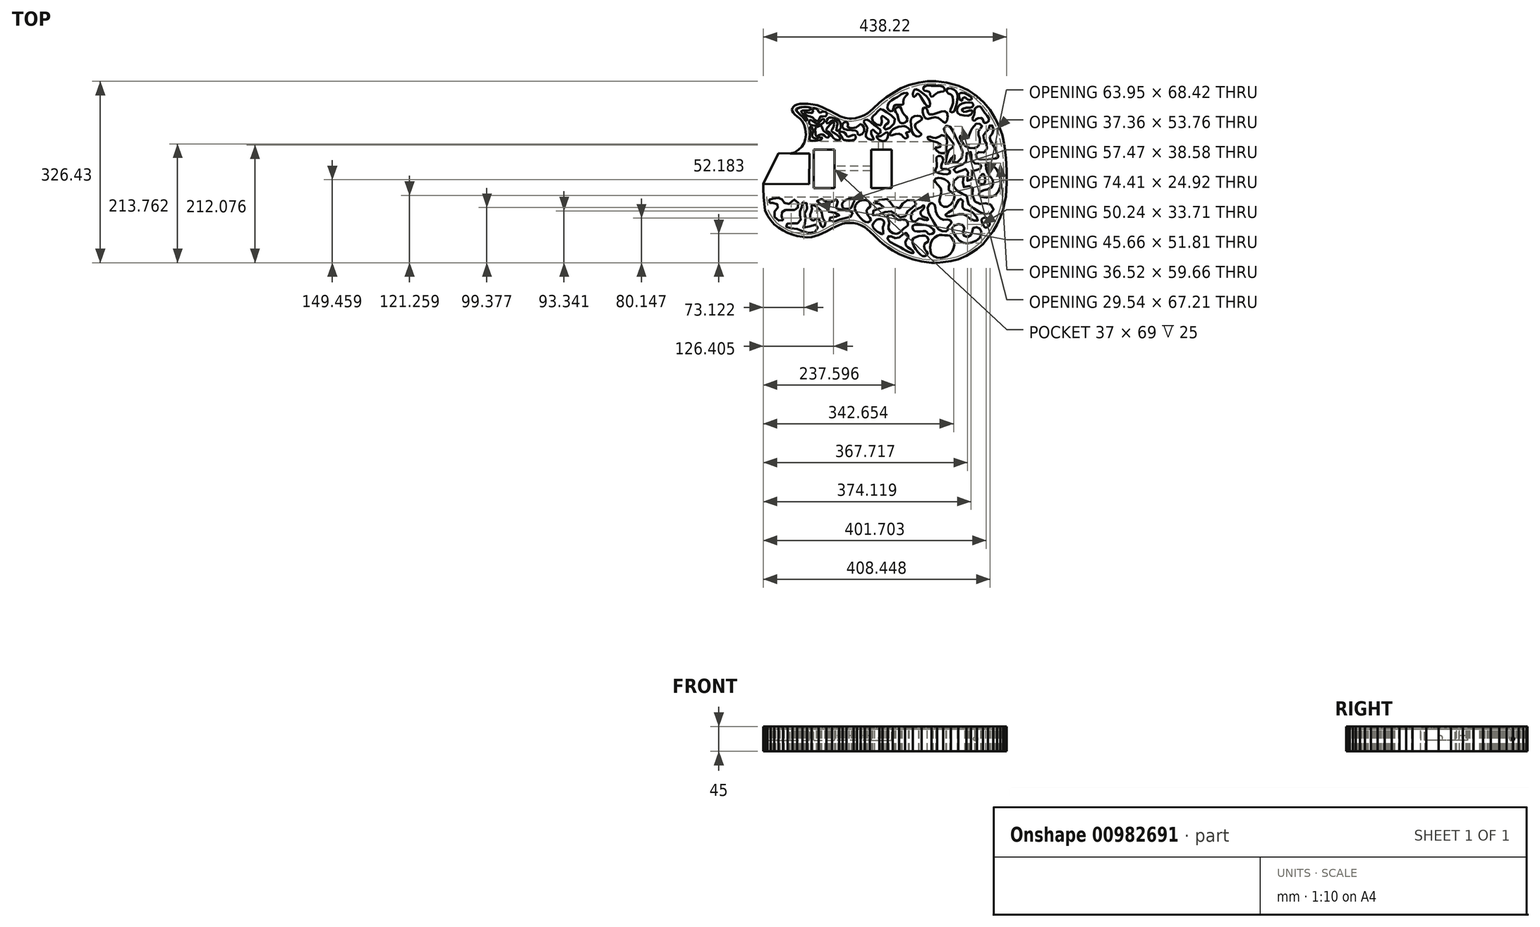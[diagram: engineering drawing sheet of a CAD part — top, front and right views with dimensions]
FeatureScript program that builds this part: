
annotation { "Feature Type Name" : "Feature", "Feature Type Description" : "" }
export const myFeature = defineFeature(function(context is Context, id is Id, definition is map)
    precondition{}
    {
        {
            var Q0;
            Q0=qCreatedBy(makeId("Top.planeOp"),FACE);
            var sketch = newSketch(context, id + "F0", { "sketchPlane" : qUnion([Q0])});
            skLineSegment(sketch, "E0", {"start": v(99.64, 0) * mm, "end": v(99.64, 10.73) * mm});
            skLineSegment(sketch, "E1", {"start": v(99.64, 10.73) * mm, "end": v(98.67, 32.9) * mm});
            skLineSegment(sketch, "E2", {"start": v(98.67, 32.9) * mm, "end": v(95.96, 54.65) * mm});
            skLineSegment(sketch, "E3", {"start": v(95.96, 54.65) * mm, "end": v(91.85, 73.91) * mm});
            skLineSegment(sketch, "E4", {"start": v(91.85, 73.91) * mm, "end": v(85.9, 91) * mm});
            skLineSegment(sketch, "E5", {"start": v(85.9, 91) * mm, "end": v(78.97, 104.86) * mm});
            skLineSegment(sketch, "E6", {"start": v(78.97, 104.86) * mm, "end": v(69.56, 119.79) * mm});
            skLineSegment(sketch, "E7", {"start": v(69.56, 119.79) * mm, "end": v(58.42, 133.1) * mm});
            skLineSegment(sketch, "E8", {"start": v(58.42, 133.1) * mm, "end": v(45.54, 144.89) * mm});
            skLineSegment(sketch, "E9", {"start": v(45.54, 144.89) * mm, "end": v(31.37, 154.73) * mm});
            skLineSegment(sketch, "E10", {"start": v(31.37, 154.73) * mm, "end": v(13.08, 163.28) * mm});
            skLineSegment(sketch, "E11", {"start": v(13.08, 163.28) * mm, "end": v(-8.34, 168.9) * mm});
            skLineSegment(sketch, "E12", {"start": v(-8.34, 168.9) * mm, "end": v(-27.06, 170.96) * mm});
            skLineSegment(sketch, "E13", {"start": v(-27.06, 170.96) * mm, "end": v(-43.5, 170.96) * mm});
            skLineSegment(sketch, "E14", {"start": v(-43.5, 170.96) * mm, "end": v(-58.54, 168.9) * mm});
            skLineSegment(sketch, "E15", {"start": v(-58.54, 168.9) * mm, "end": v(-77.15, 164.04) * mm});
            skLineSegment(sketch, "E16", {"start": v(-77.15, 164.04) * mm, "end": v(-90.67, 158.41) * mm});
            skLineSegment(sketch, "E17", {"start": v(-90.67, 158.41) * mm, "end": v(-102.57, 151.81) * mm});
            skLineSegment(sketch, "E18", {"start": v(-102.57, 151.81) * mm, "end": v(-117.4, 141.86) * mm});
            skLineSegment(sketch, "E19", {"start": v(-117.4, 141.86) * mm, "end": v(-129.08, 132.88) * mm});
            skLineSegment(sketch, "E20", {"start": v(-129.08, 132.88) * mm, "end": v(-141.3, 121.73) * mm});
            skLineSegment(sketch, "E21", {"start": v(-141.3, 121.73) * mm, "end": v(-150.5, 113.73) * mm});
            skLineSegment(sketch, "E22", {"start": v(-150.5, 113.73) * mm, "end": v(-157.64, 109.5) * mm});
            skLineSegment(sketch, "E23", {"start": v(-157.64, 109.5) * mm, "end": v(-164.24, 106.91) * mm});
            skLineSegment(sketch, "E24", {"start": v(-164.24, 106.91) * mm, "end": v(-172.58, 104.86) * mm});
            skLineSegment(sketch, "E25", {"start": v(-172.58, 104.86) * mm, "end": v(-179.46, 103.91) * mm});
            skLineSegment(sketch, "E26", {"start": v(-179.46, 103.91) * mm, "end": v(-183.84, 103.91) * mm});
            skLineSegment(sketch, "E27", {"start": v(-183.84, 103.91) * mm, "end": v(-191.3, 105.29) * mm});
            skLineSegment(sketch, "E28", {"start": v(-191.3, 105.29) * mm, "end": v(-199.42, 107.78) * mm});
            skLineSegment(sketch, "E29", {"start": v(-199.42, 107.78) * mm, "end": v(-207.97, 112.1) * mm});
            skLineSegment(sketch, "E30", {"start": v(-207.97, 112.1) * mm, "end": v(-218.68, 118.16) * mm});
            skLineSegment(sketch, "E31", {"start": v(-218.68, 118.16) * mm, "end": v(-225.4, 121.4) * mm});
            skLineSegment(sketch, "E32", {"start": v(-225.4, 121.4) * mm, "end": v(-233.3, 124.87) * mm});
            skLineSegment(sketch, "E33", {"start": v(-233.3, 124.87) * mm, "end": v(-241.3, 127.8) * mm});
            skLineSegment(sketch, "E34", {"start": v(-241.3, 127.8) * mm, "end": v(-249.1, 129.41) * mm});
            skLineSegment(sketch, "E35", {"start": v(-249.1, 129.41) * mm, "end": v(-257.75, 130.5) * mm});
            skLineSegment(sketch, "E36", {"start": v(-257.75, 130.5) * mm, "end": v(-265.86, 130.5) * mm});
            skLineSegment(sketch, "E37", {"start": v(-265.86, 130.5) * mm, "end": v(-272.14, 130.5) * mm});
            skLineSegment(sketch, "E38", {"start": v(-272.14, 130.5) * mm, "end": v(-277.44, 129.2) * mm});
            skLineSegment(sketch, "E39", {"start": v(-277.44, 129.2) * mm, "end": v(-281.88, 127.25) * mm});
            skLineSegment(sketch, "E40", {"start": v(-281.88, 127.25) * mm, "end": v(-284.58, 125.09) * mm});
            skLineSegment(sketch, "E41", {"start": v(-284.58, 125.09) * mm, "end": v(-285.88, 122.7) * mm});
            skLineSegment(sketch, "E42", {"start": v(-285.88, 122.7) * mm, "end": v(-286.97, 120.11) * mm});
            skLineSegment(sketch, "E43", {"start": v(-286.97, 120.11) * mm, "end": v(-286.2, 118.16) * mm});
            skLineSegment(sketch, "E44", {"start": v(-286.2, 118.16) * mm, "end": v(-284.7, 114.92) * mm});
            skLineSegment(sketch, "E45", {"start": v(-284.7, 114.92) * mm, "end": v(-281.77, 111.89) * mm});
            skLineSegment(sketch, "E46", {"start": v(-281.77, 111.89) * mm, "end": v(-277.44, 107.88) * mm});
            skLineSegment(sketch, "E47", {"start": v(-277.44, 107.88) * mm, "end": v(-272.68, 103.88) * mm});
            skLineSegment(sketch, "E48", {"start": v(-272.68, 103.88) * mm, "end": v(-268.03, 98.58) * mm});
            skLineSegment(sketch, "E49", {"start": v(-268.03, 98.58) * mm, "end": v(-264.57, 92.41) * mm});
            skLineSegment(sketch, "E50", {"start": v(-264.57, 92.41) * mm, "end": v(-262.73, 85.38) * mm});
            skLineSegment(sketch, "E51", {"start": v(-262.73, 85.38) * mm, "end": v(-261.78, 74.51) * mm});
            skLineSegment(sketch, "E52", {"start": v(-261.78, 74.51) * mm, "end": v(-262.75, 67.05) * mm});
            skLineSegment(sketch, "E53", {"start": v(-262.75, 67.05) * mm, "end": v(-264, 63.33) * mm});
            skLineSegment(sketch, "E54", {"start": v(-265.13, 60.01) * mm, "end": v(-269.24, 53.2) * mm});
            skLineSegment(sketch, "E55", {"start": v(-269.24, 53.2) * mm, "end": v(-274.98, 48) * mm});
            skLineSegment(sketch, "E56", {"start": v(-274.98, 48) * mm, "end": v(-282.23, 43.24) * mm});
            skLineSegment(sketch, "E57", {"start": v(-282.23, 43.24) * mm, "end": v(-290.16, 41.2) * mm});
            skLineSegment(sketch, "E58", {"start": v(-311.14, 41.44) * mm, "end": v(-338.55, -13.56) * mm});
            skLineSegment(sketch, "E59", {"start": v(-338.55, -13.56) * mm, "end": v(-338.55, -21.68) * mm});
            skLineSegment(sketch, "E60", {"start": v(-338.55, -21.68) * mm, "end": v(-337.73, -37.51) * mm});
            skLineSegment(sketch, "E61", {"start": v(-335.04, -61.02) * mm, "end": v(-330.72, -70.54) * mm});
            skLineSegment(sketch, "E62", {"start": v(-330.72, -70.54) * mm, "end": v(-325.2, -79.1) * mm});
            skLineSegment(sketch, "E63", {"start": v(-325.2, -79.1) * mm, "end": v(-318.81, -86.34) * mm});
            skLineSegment(sketch, "E64", {"start": v(-318.81, -86.34) * mm, "end": v(-311.14, -92.56) * mm});
            skLineSegment(sketch, "E65", {"start": v(-311.14, -92.56) * mm, "end": v(-302.73, -97.47) * mm});
            skLineSegment(sketch, "E66", {"start": v(-302.73, -97.47) * mm, "end": v(-294.86, -101.8) * mm});
            skLineSegment(sketch, "E67", {"start": v(-294.86, -101.8) * mm, "end": v(-286.1, -105.26) * mm});
            skLineSegment(sketch, "E68", {"start": v(-286.1, -105.26) * mm, "end": v(-277.44, -107.2) * mm});
            skLineSegment(sketch, "E69", {"start": v(-277.44, -107.2) * mm, "end": v(-268.15, -109.07) * mm});
            skLineSegment(sketch, "E70", {"start": v(-268.15, -109.07) * mm, "end": v(-259.64, -109.9) * mm});
            skLineSegment(sketch, "E71", {"start": v(-259.64, -109.9) * mm, "end": v(-251.7, -109.38) * mm});
            skLineSegment(sketch, "E72", {"start": v(-251.7, -109.38) * mm, "end": v(-238.5, -105.78) * mm});
            skLineSegment(sketch, "E73", {"start": v(-238.5, -105.78) * mm, "end": v(-224.86, -99.4) * mm});
            skLineSegment(sketch, "E74", {"start": v(-224.86, -99.4) * mm, "end": v(-214.58, -93.23) * mm});
            skLineSegment(sketch, "E75", {"start": v(-214.58, -93.23) * mm, "end": v(-201.7, -87.6) * mm});
            skLineSegment(sketch, "E76", {"start": v(-201.7, -87.6) * mm, "end": v(-195.32, -85.22) * mm});
            skLineSegment(sketch, "E77", {"start": v(-195.32, -85.22) * mm, "end": v(-188.5, -83.7) * mm});
            skLineSegment(sketch, "E78", {"start": v(-188.5, -83.7) * mm, "end": v(-182, -83.7) * mm});
            skLineSegment(sketch, "E79", {"start": v(-182, -83.7) * mm, "end": v(-175.95, -83.7) * mm});
            skLineSegment(sketch, "E80", {"start": v(-175.95, -83.7) * mm, "end": v(-169.78, -85.33) * mm});
            skLineSegment(sketch, "E81", {"start": v(-169.78, -85.33) * mm, "end": v(-162.96, -88.03) * mm});
            skLineSegment(sketch, "E82", {"start": v(-162.96, -88.03) * mm, "end": v(-155.93, -91.82) * mm});
            skLineSegment(sketch, "E83", {"start": v(-155.93, -91.82) * mm, "end": v(-146.95, -98.96) * mm});
            skLineSegment(sketch, "E84", {"start": v(-146.95, -98.96) * mm, "end": v(-138.61, -107.08) * mm});
            skLineSegment(sketch, "E85", {"start": v(-138.61, -107.08) * mm, "end": v(-129.85, -115.62) * mm});
            skLineSegment(sketch, "E86", {"start": v(-129.85, -115.62) * mm, "end": v(-123.57, -120.92) * mm});
            skLineSegment(sketch, "E87", {"start": v(-123.57, -120.92) * mm, "end": v(-114.59, -127.63) * mm});
            skLineSegment(sketch, "E88", {"start": v(-114.59, -127.63) * mm, "end": v(-105.4, -133.48) * mm});
            skLineSegment(sketch, "E89", {"start": v(-105.4, -133.48) * mm, "end": v(-94.14, -139.75) * mm});
            skLineSegment(sketch, "E90", {"start": v(-94.14, -139.75) * mm, "end": v(-83.53, -144.62) * mm});
            skLineSegment(sketch, "E91", {"start": v(-83.53, -144.62) * mm, "end": v(-69.47, -149.7) * mm});
            skLineSegment(sketch, "E92", {"start": v(-69.47, -149.7) * mm, "end": v(-53.67, -153.5) * mm});
            skLineSegment(sketch, "E93", {"start": v(-53.67, -153.5) * mm, "end": v(-43.93, -154.57) * mm});
            skLineSegment(sketch, "E94", {"start": v(-43.93, -154.57) * mm, "end": v(-35.83, -155.47) * mm});
            skLineSegment(sketch, "E95", {"start": v(-35.83, -155.47) * mm, "end": v(-25.53, -155.47) * mm});
            skLineSegment(sketch, "E96", {"start": v(-25.53, -155.47) * mm, "end": v(-14.82, -154.57) * mm});
            skLineSegment(sketch, "E97", {"start": v(-14.82, -154.57) * mm, "end": v(-0.86, -152.73) * mm});
            skLineSegment(sketch, "E98", {"start": v(-0.86, -152.73) * mm, "end": v(12.77, -149.27) * mm});
            skLineSegment(sketch, "E99", {"start": v(12.77, -149.27) * mm, "end": v(27.17, -143.32) * mm});
            skLineSegment(sketch, "E100", {"start": v(27.17, -143.32) * mm, "end": v(35.82, -138.24) * mm});
            skLineSegment(sketch, "E101", {"start": v(35.82, -138.24) * mm, "end": v(46.43, -130.77) * mm});
            skLineSegment(sketch, "E102", {"start": v(46.43, -130.77) * mm, "end": v(56.82, -122.12) * mm});
            skLineSegment(sketch, "E103", {"start": v(56.82, -122.12) * mm, "end": v(66.34, -110.97) * mm});
            skLineSegment(sketch, "E104", {"start": v(66.34, -110.97) * mm, "end": v(75.32, -98.85) * mm});
            skLineSegment(sketch, "E105", {"start": v(75.32, -98.85) * mm, "end": v(82.68, -86.3) * mm});
            skLineSegment(sketch, "E106", {"start": v(82.68, -86.3) * mm, "end": v(88.2, -73.97) * mm});
            skLineSegment(sketch, "E107", {"start": v(88.2, -73.97) * mm, "end": v(93.18, -59.69) * mm});
            skLineSegment(sketch, "E108", {"start": v(93.18, -59.69) * mm, "end": v(96.1, -47.35) * mm});
            skLineSegment(sketch, "E109", {"start": v(96.1, -47.35) * mm, "end": v(98.37, -36.1) * mm});
            skLineSegment(sketch, "E110", {"start": v(98.37, -36.1) * mm, "end": v(99.67, -11.33) * mm});
            skLineSegment(sketch, "E111", {"start": v(99.67, -11.33) * mm, "end": v(99.64, 0) * mm});
            skLineSegment(sketch, "E112", {"start": v(-311.14, 41.44) * mm, "end": v(-276.44, 41.06) * mm});
            skLineSegment(sketch, "E113", {"start": v(-255.37, 40.83) * mm, "end": v(-255.97, -14.3) * mm});
            skLineSegment(sketch, "E114", {"start": v(-338.55, -13.56) * mm, "end": v(-255.97, -14.3) * mm});
            skLineSegment(sketch, "E115.bottom", {"start": v(-247.47, 47.83) * mm, "end": v(-210.47, 47.83) * mm});
            skLineSegment(sketch, "E115.top", {"start": v(-247.47, -21.17) * mm, "end": v(-210.47, -21.17) * mm});
            skLineSegment(sketch, "E115.left", {"start": v(-247.47, 47.83) * mm, "end": v(-247.47, -21.17) * mm});
            skLineSegment(sketch, "E115.right", {"start": v(-210.47, 47.83) * mm, "end": v(-210.47, -21.17) * mm});
            skLineSegment(sketch, "E116.bottom", {"start": v(-144.47, 47.83) * mm, "end": v(-107.47, 47.83) * mm});
            skLineSegment(sketch, "E116.top", {"start": v(-144.47, -21.17) * mm, "end": v(-107.47, -21.17) * mm});
            skLineSegment(sketch, "E116.left", {"start": v(-144.47, 47.83) * mm, "end": v(-144.47, -21.17) * mm});
            skLineSegment(sketch, "E116.right", {"start": v(-107.47, 47.83) * mm, "end": v(-107.47, -21.17) * mm});
            skLineSegment(sketch, "E117.top", {"start": v(-32.47, -37.51) * mm, "end": v(-337.73, -37.51) * mm});
            skLineSegment(sketch, "E117.left", {"start": v(-32.47, 62.49) * mm, "end": v(-32.47, -37.51) * mm});
            skLineSegment(sketch, "E118", {"start": v(-337.73, -37.51) * mm, "end": v(-335.04, -61.02) * mm});
            skLineSegment(sketch, "E119", {"start": v(-264, 63.33) * mm, "end": v(-265.13, 60.01) * mm});
            skLineSegment(sketch, "E120", {"start": v(-264, 63.33) * mm, "end": v(-32.47, 62.49) * mm});
            skLineSegment(sketch, "E121.2", {"start": v(-265.34, 49.98) * mm, "end": v(-271.91, 44.04) * mm});
            skLineSegment(sketch, "E121.3", {"start": v(-260.57, 57.9) * mm, "end": v(-265.34, 49.98) * mm});
            skLineSegment(sketch, "E121.4", {"start": v(-259.27, 61.73) * mm, "end": v(-260.57, 57.9) * mm});
            skLineSegment(sketch, "E121.5", {"start": v(-257.86, 65.9) * mm, "end": v(-259.27, 61.73) * mm});
            skLineSegment(sketch, "E121.6", {"start": v(-256.75, 74.4) * mm, "end": v(-257.86, 65.9) * mm});
            skLineSegment(sketch, "E121.7", {"start": v(-257.78, 86.24) * mm, "end": v(-256.75, 74.4) * mm});
            skLineSegment(sketch, "E121.8", {"start": v(-259.9, 94.3) * mm, "end": v(-257.78, 86.24) * mm});
            skLineSegment(sketch, "E121.9", {"start": v(-263.93, 101.48) * mm, "end": v(-259.9, 94.3) * mm});
            skLineSegment(sketch, "E121.10", {"start": v(-269.17, 107.46) * mm, "end": v(-263.93, 101.48) * mm});
            skLineSegment(sketch, "E121.11", {"start": v(-274.13, 111.64) * mm, "end": v(-269.17, 107.46) * mm});
            skLineSegment(sketch, "E121.12", {"start": v(-278.27, 115.46) * mm, "end": v(-274.13, 111.64) * mm});
            skLineSegment(sketch, "E121.13", {"start": v(-280.52, 117.79) * mm, "end": v(-278.27, 115.46) * mm});
            skLineSegment(sketch, "E121.14", {"start": v(-281.57, 120.05) * mm, "end": v(-280.52, 117.79) * mm});
            skLineSegment(sketch, "E121.15", {"start": v(-281.37, 120.54) * mm, "end": v(-281.57, 120.05) * mm});
            skLineSegment(sketch, "E121.16", {"start": v(-280.68, 121.81) * mm, "end": v(-281.37, 120.54) * mm});
            skLineSegment(sketch, "E121.17", {"start": v(-279.27, 122.94) * mm, "end": v(-280.68, 121.81) * mm});
            skLineSegment(sketch, "E121.18", {"start": v(-275.83, 124.45) * mm, "end": v(-279.27, 122.94) * mm});
            skLineSegment(sketch, "E121.19", {"start": v(-271.54, 125.5) * mm, "end": v(-275.83, 124.45) * mm});
            skLineSegment(sketch, "E121.20", {"start": v(-265.86, 125.5) * mm, "end": v(-271.54, 125.5) * mm});
            skLineSegment(sketch, "E121.21", {"start": v(-258.06, 125.5) * mm, "end": v(-265.86, 125.5) * mm});
            skLineSegment(sketch, "E121.22", {"start": v(-249.91, 124.48) * mm, "end": v(-258.06, 125.5) * mm});
            skLineSegment(sketch, "E121.23", {"start": v(-242.67, 122.97) * mm, "end": v(-249.91, 124.48) * mm});
            skLineSegment(sketch, "E121.24", {"start": v(-235.15, 120.23) * mm, "end": v(-242.67, 122.97) * mm});
            skLineSegment(sketch, "E121.25", {"start": v(-227.49, 116.87) * mm, "end": v(-235.15, 120.23) * mm});
            skLineSegment(sketch, "E121.26", {"start": v(-221, 113.73) * mm, "end": v(-227.49, 116.87) * mm});
            skLineSegment(sketch, "E121.27", {"start": v(-210.33, 107.7) * mm, "end": v(-221, 113.73) * mm});
            skLineSegment(sketch, "E121.28", {"start": v(-201.3, 103.12) * mm, "end": v(-210.33, 107.7) * mm});
            skLineSegment(sketch, "E121.29", {"start": v(-192.5, 100.42) * mm, "end": v(-201.3, 103.12) * mm});
            skLineSegment(sketch, "E121.30", {"start": v(-184.3, 98.91) * mm, "end": v(-192.5, 100.42) * mm});
            skLineSegment(sketch, "E121.31", {"start": v(-179.12, 98.91) * mm, "end": v(-184.3, 98.91) * mm});
            skLineSegment(sketch, "E121.32", {"start": v(-171.64, 99.94) * mm, "end": v(-179.12, 98.91) * mm});
            skLineSegment(sketch, "E121.33", {"start": v(-162.72, 102.14) * mm, "end": v(-171.64, 99.94) * mm});
            skLineSegment(sketch, "E121.34", {"start": v(-155.44, 105) * mm, "end": v(-162.72, 102.14) * mm});
            skLineSegment(sketch, "E121.35", {"start": v(-147.57, 109.66) * mm, "end": v(-155.44, 105) * mm});
            skLineSegment(sketch, "E121.36", {"start": v(-137.98, 118) * mm, "end": v(-147.57, 109.66) * mm});
            skLineSegment(sketch, "E121.37", {"start": v(-125.87, 129.04) * mm, "end": v(-137.98, 118) * mm});
            skLineSegment(sketch, "E121.38", {"start": v(-114.48, 137.8) * mm, "end": v(-125.87, 129.04) * mm});
            skLineSegment(sketch, "E121.39", {"start": v(-99.96, 147.54) * mm, "end": v(-114.48, 137.8) * mm});
            skLineSegment(sketch, "E121.40", {"start": v(71.14, -96.1) * mm, "end": v(78.23, -84.01) * mm});
            skLineSegment(sketch, "E121.41", {"start": v(62.43, -107.85) * mm, "end": v(71.14, -96.1) * mm});
            skLineSegment(sketch, "E121.42", {"start": v(53.3, -118.54) * mm, "end": v(62.43, -107.85) * mm});
            skLineSegment(sketch, "E121.43", {"start": v(43.38, -126.8) * mm, "end": v(53.3, -118.54) * mm});
            skLineSegment(sketch, "E121.44", {"start": v(33.11, -134.03) * mm, "end": v(43.38, -126.8) * mm});
            skLineSegment(sketch, "E121.45", {"start": v(24.93, -138.83) * mm, "end": v(33.11, -134.03) * mm});
            skLineSegment(sketch, "E121.46", {"start": v(11.2, -144.51) * mm, "end": v(24.93, -138.83) * mm});
            skLineSegment(sketch, "E121.47", {"start": v(-1.8, -147.82) * mm, "end": v(11.2, -144.51) * mm});
            skLineSegment(sketch, "E121.48", {"start": v(-15.36, -149.6) * mm, "end": v(-1.8, -147.82) * mm});
            skLineSegment(sketch, "E121.49", {"start": v(-25.74, -150.47) * mm, "end": v(-15.36, -149.6) * mm});
            skLineSegment(sketch, "E121.50", {"start": v(-35.55, -150.47) * mm, "end": v(-25.74, -150.47) * mm});
            skLineSegment(sketch, "E121.51", {"start": v(-43.38, -149.6) * mm, "end": v(-35.55, -150.47) * mm});
            skLineSegment(sketch, "E121.52", {"start": v(-120.46, -117) * mm, "end": v(-111.75, -123.51) * mm});
            skLineSegment(sketch, "E121.53", {"start": v(-126.48, -111.92) * mm, "end": v(-120.46, -117) * mm});
            skLineSegment(sketch, "E121.54", {"start": v(-135.12, -103.5) * mm, "end": v(-126.48, -111.92) * mm});
            skLineSegment(sketch, "E121.55", {"start": v(-143.64, -95.2) * mm, "end": v(-135.12, -103.5) * mm});
            skLineSegment(sketch, "E121.56", {"start": v(-111.75, -123.51) * mm, "end": v(-102.83, -129.18) * mm});
            skLineSegment(sketch, "E121.57", {"start": v(-102.83, -129.18) * mm, "end": v(-91.87, -135.29) * mm});
            skLineSegment(sketch, "E121.58", {"start": v(-91.87, -135.29) * mm, "end": v(-81.64, -139.99) * mm});
            skLineSegment(sketch, "E121.59", {"start": v(-81.64, -139.99) * mm, "end": v(-68.03, -144.9) * mm});
            skLineSegment(sketch, "E121.60", {"start": v(-68.03, -144.9) * mm, "end": v(-52.8, -148.56) * mm});
            skLineSegment(sketch, "E121.61", {"start": v(-52.8, -148.56) * mm, "end": v(-43.38, -149.6) * mm});
            skLineSegment(sketch, "E121.62", {"start": v(78.23, -84.01) * mm, "end": v(83.55, -72.12) * mm});
            skLineSegment(sketch, "E121.63", {"start": v(83.55, -72.12) * mm, "end": v(88.37, -58.28) * mm});
            skLineSegment(sketch, "E121.64", {"start": v(88.37, -58.28) * mm, "end": v(91.21, -46.28) * mm});
            skLineSegment(sketch, "E121.65", {"start": v(91.21, -46.28) * mm, "end": v(93.4, -35.47) * mm});
            skLineSegment(sketch, "E121.66", {"start": v(93.4, -35.47) * mm, "end": v(94.67, -11.2) * mm});
            skLineSegment(sketch, "E121.67", {"start": v(94.67, -11.2) * mm, "end": v(94.64, 0) * mm});
            skLineSegment(sketch, "E121.68", {"start": v(94.64, 0) * mm, "end": v(94.64, 10.62) * mm});
            skLineSegment(sketch, "E121.69", {"start": v(94.64, 10.62) * mm, "end": v(93.68, 32.49) * mm});
            skLineSegment(sketch, "E121.70", {"start": v(93.68, 32.49) * mm, "end": v(91.03, 53.82) * mm});
            skLineSegment(sketch, "E121.71", {"start": v(91.03, 53.82) * mm, "end": v(87.02, 72.56) * mm});
            skLineSegment(sketch, "E121.72", {"start": v(87.02, 72.56) * mm, "end": v(81.28, 89.06) * mm});
            skLineSegment(sketch, "E121.73", {"start": v(81.28, 89.06) * mm, "end": v(74.61, 102.4) * mm});
            skLineSegment(sketch, "E121.74", {"start": v(74.61, 102.4) * mm, "end": v(65.51, 116.83) * mm});
            skLineSegment(sketch, "E121.75", {"start": v(65.51, 116.83) * mm, "end": v(54.8, 129.63) * mm});
            skLineSegment(sketch, "E121.76", {"start": v(54.8, 129.63) * mm, "end": v(42.41, 140.97) * mm});
            skLineSegment(sketch, "E121.77", {"start": v(42.41, 140.97) * mm, "end": v(28.87, 150.38) * mm});
            skLineSegment(sketch, "E121.78", {"start": v(28.87, 150.38) * mm, "end": v(11.38, 158.56) * mm});
            skLineSegment(sketch, "E121.79", {"start": v(11.38, 158.56) * mm, "end": v(-9.25, 163.98) * mm});
            skLineSegment(sketch, "E121.80", {"start": v(-9.25, 163.98) * mm, "end": v(-27.33, 165.96) * mm});
            skLineSegment(sketch, "E121.81", {"start": v(-27.33, 165.96) * mm, "end": v(-43.16, 165.96) * mm});
            skLineSegment(sketch, "E121.82", {"start": v(-43.16, 165.96) * mm, "end": v(-57.56, 164) * mm});
            skLineSegment(sketch, "E121.83", {"start": v(-57.56, 164) * mm, "end": v(-75.55, 159.29) * mm});
            skLineSegment(sketch, "E121.84", {"start": v(-75.55, 159.29) * mm, "end": v(-88.5, 153.9) * mm});
            skLineSegment(sketch, "E121.85", {"start": v(-88.5, 153.9) * mm, "end": v(-99.96, 147.54) * mm});
            skLineSegment(sketch, "E122.0", {"start": v(-153.16, -87.63) * mm, "end": v(-143.64, -95.2) * mm});
            skLineSegment(sketch, "E122.1", {"start": v(-160.85, -83.5) * mm, "end": v(-153.16, -87.63) * mm});
            skLineSegment(sketch, "E122.2", {"start": v(-168.21, -80.57) * mm, "end": v(-160.85, -83.5) * mm});
            skLineSegment(sketch, "E122.3", {"start": v(-175.3, -78.7) * mm, "end": v(-168.21, -80.57) * mm});
            skLineSegment(sketch, "E122.4", {"start": v(-182, -78.7) * mm, "end": v(-175.3, -78.7) * mm});
            skLineSegment(sketch, "E122.5", {"start": v(-252.53, -104.42) * mm, "end": v(-240.22, -101.07) * mm});
            skLineSegment(sketch, "E122.6", {"start": v(-259.56, -104.89) * mm, "end": v(-252.53, -104.42) * mm});
            skLineSegment(sketch, "E122.7", {"start": v(-267.41, -104.12) * mm, "end": v(-259.56, -104.89) * mm});
            skLineSegment(sketch, "E122.8", {"start": v(-276.4, -102.31) * mm, "end": v(-267.41, -104.12) * mm});
            skLineSegment(sketch, "E122.9", {"start": v(-240.22, -101.07) * mm, "end": v(-227.2, -94.97) * mm});
            skLineSegment(sketch, "E122.10", {"start": v(-227.2, -94.97) * mm, "end": v(-216.87, -88.77) * mm});
            skLineSegment(sketch, "E122.11", {"start": v(-216.87, -88.77) * mm, "end": v(-203.58, -82.96) * mm});
            skLineSegment(sketch, "E122.12", {"start": v(-203.58, -82.96) * mm, "end": v(-196.74, -80.42) * mm});
            skLineSegment(sketch, "E122.13", {"start": v(-196.74, -80.42) * mm, "end": v(-189.05, -78.7) * mm});
            skLineSegment(sketch, "E122.14", {"start": v(-189.05, -78.7) * mm, "end": v(-182, -78.7) * mm});
            skLineSegment(sketch, "E123.0", {"start": v(-284.62, -100.46) * mm, "end": v(-276.4, -102.31) * mm});
            skLineSegment(sketch, "E123.1", {"start": v(-292.73, -97.26) * mm, "end": v(-284.62, -100.46) * mm});
            skLineSegment(sketch, "E123.2", {"start": v(-300.26, -93.12) * mm, "end": v(-292.73, -97.26) * mm});
            skLineSegment(sketch, "E123.3", {"start": v(-308.29, -88.44) * mm, "end": v(-300.26, -93.12) * mm});
            skLineSegment(sketch, "E123.4", {"start": v(-315.34, -82.72) * mm, "end": v(-308.29, -88.44) * mm});
            skLineSegment(sketch, "E123.5", {"start": v(-332.7, -37.51) * mm, "end": v(-330.17, -59.67) * mm});
            skLineSegment(sketch, "E123.6", {"start": v(-330.17, -59.67) * mm, "end": v(-326.32, -68.14) * mm});
            skLineSegment(sketch, "E123.7", {"start": v(-326.32, -68.14) * mm, "end": v(-321.2, -76.07) * mm});
            skLineSegment(sketch, "E123.8", {"start": v(-321.2, -76.07) * mm, "end": v(-315.34, -82.72) * mm});
            skLineSegment(sketch, "E124", {"start": v(-276.44, 41.06) * mm, "end": v(-255.37, 40.83) * mm});
            skLineSegment(sketch, "E125", {"start": v(-271.91, 44.04) * mm, "end": v(-276.44, 41.06) * mm});
            skSolve(sketch);
        }
        {
            var Q0;
            {var subQ1=sQuery(id+"F0.wireOp",EDGE,"E117.left");Q0=makeQuery(id+"F0.imprint","IMPRINT",FACE,{"disambiguationData":[TD([[makeQuery(id+"F0.imprint","IMPRINT",EDGE,{"derivedFrom":subQ1}),1.0]])]});}
            extrude(context, id + "F1", {"entities" : qUnion([Q0]), "oppositeDirection" : true, "depth" : 5 * mm, "offsetDistance" : 25 * mm});
        }
        {
            var Q0;
            Q0=makeQuery(id+"F0.imprint","IMPRINT",FACE,{"disambiguationData":[TD([[makeQuery(id+"F0.imprint","IMPRINT",EDGE,{"derivedFrom":sQuery(id+"F0.wireOp",EDGE,"E116.bottom")}),-1.0]])]});
            var Q1;
            Q1=makeQuery(id+"F0.imprint","IMPRINT",FACE,{"disambiguationData":[TD([[makeQuery(id+"F0.imprint","IMPRINT",EDGE,{"derivedFrom":sQuery(id+"F0.wireOp",EDGE,"E115.bottom")}),-1.0]])]});
            var Q2;
            {var subQ2=sQuery(id+"F0.wireOp",EDGE,"E58");Q2=makeQuery(id+"F0.imprint","IMPRINT",FACE,{"disambiguationData":[TD([[makeQuery(id+"F0.imprint","IMPRINT",EDGE,{"derivedFrom":subQ2}),1.0]])]});}
            var Q3;
            Q3=makeQuery(id+"F0.imprint","IMPRINT",FACE,{"disambiguationData":[TD([[makeQuery(id+"F0.imprint","IMPRINT",EDGE,{"derivedFrom":sQuery(id+"F0.wireOp",EDGE,"E54")}),1.0]])]});
            var Q4;
            Q4=makeQuery(id+"F0.imprint","IMPRINT",FACE,{"disambiguationData":[TD([[makeQuery(id+"F0.imprint","IMPRINT",EDGE,{"derivedFrom":sQuery(id+"F0.wireOp",EDGE,"E0")}),1.0]])]});
            var Q5;
            Q5=makeQuery(id+"F0.imprint","IMPRINT",FACE,{"disambiguationData":[TD([[makeQuery(id+"F0.imprint","IMPRINT",EDGE,{"derivedFrom":sQuery(id+"F0.wireOp",EDGE,"E59")}),1.0]])]});
            extrude(context, id + "F2", {"entities" : qUnion([Q0, Q1, Q2, Q3, Q4, Q5]), "operationType" : NewBodyOperationType.ADD, "oppositeDirection" : true, "depth" : 45 * mm, "offsetDistance" : 25 * mm});
        }
        {
            var Q0;
            {var subQ3=sQuery(id+"F0.wireOp",EDGE,"E58");Q0=makeQuery(id+"F0.imprint","IMPRINT",FACE,{"disambiguationData":[TD([[makeQuery(id+"F0.imprint","IMPRINT",EDGE,{"derivedFrom":subQ3}),1.0]])]});}
            var Q1;
            Q1=makeQuery(id+"F0.imprint","IMPRINT",FACE,{"disambiguationData":[TD([[makeQuery(id+"F0.imprint","IMPRINT",EDGE,{"derivedFrom":sQuery(id+"F0.wireOp",EDGE,"E115.bottom")}),-1.0]])]});
            var Q2;
            Q2=makeQuery(id+"F0.imprint","IMPRINT",FACE,{"disambiguationData":[TD([[makeQuery(id+"F0.imprint","IMPRINT",EDGE,{"derivedFrom":sQuery(id+"F0.wireOp",EDGE,"E116.bottom")}),-1.0]])]});
            extrude(context, id + "F3", {"entities" : qUnion([Q0, Q1, Q2]), "operationType" : NewBodyOperationType.REMOVE, "oppositeDirection" : true, "depth" : 25 * mm, "offsetDistance" : 25 * mm});
        }
        {
            var Q0;
            Q0=makeQuery(id+"F0.imprint","IMPRINT",FACE,{"disambiguationData":[TD([[makeQuery(id+"F0.imprint","IMPRINT",EDGE,{"derivedFrom":sQuery(id+"F0.wireOp",EDGE,"E0")}),1.0]])]});
            var sketch = newSketch(context, id + "F4", { "sketchPlane" : qUnion([Q0])});
            skFitSpline(sketch, "E126", {"points": [v(-246.67, 91.44) * mm, v(-255.37, 94.7) * mm, v(-254.1, 101.73) * mm, v(-241.7, 95.17) * mm, v(-232.1, 102.95) * mm, v(-228.07, 100.65) * mm, v(-233.02, 94.58) * mm, v(-246.67, 91.44) * mm]});
            skFitSpline(sketch, "E127", {"points": [v(-258.94, 109.16) * mm, v(-251.4, 107.22) * mm, v(-244.58, 100.33) * mm, v(-241.6, 99.56) * mm, v(-238.44, 101.73) * mm, v(-235.53, 107.77) * mm, v(-226.8, 107.66) * mm, v(-223.68, 113.46) * mm, v(-230.26, 116.77) * mm, v(-237.78, 114.71) * mm, v(-240.12, 120) * mm, v(-248.96, 122.42) * mm, v(-249.1, 116) * mm, v(-255.82, 113.94) * mm, v(-264.55, 115.33) * mm, v(-258.94, 109.16) * mm]});
            skFitSpline(sketch, "E128", {"points": [v(-255.87, 119.1) * mm, v(-252.32, 121.73) * mm, v(-256.46, 124.17) * mm, v(-265.55, 124.75) * mm, v(-273.37, 123.7) * mm, v(-278.9, 119.25) * mm, v(-269.9, 109.16) * mm, v(-261.8, 100.15) * mm, v(-258.94, 101.73) * mm, v(-261.8, 105.93) * mm, v(-267.11, 111.9) * mm, v(-270.06, 117.75) * mm, v(-255.87, 119.1) * mm]});
            skFitSpline(sketch, "E129", {"points": [v(-253.77, 75.85) * mm, v(-253.77, 83.98) * mm, v(-255.18, 86.65) * mm, v(-253.91, 89.03) * mm, v(-249.85, 85.38) * mm, v(-248.44, 81.46) * mm, v(-250.4, 72.48) * mm, v(-243.25, 67.85) * mm, v(-237.78, 70.38) * mm, v(-232.45, 69.11) * mm, v(-236.66, 65.05) * mm, v(-245.64, 64.34) * mm, v(-253.07, 64.34) * mm, v(-255.04, 66.45) * mm, v(-253.77, 75.85) * mm]});
            skFitSpline(sketch, "E130", {"points": [v(-228.8, 73.74) * mm, v(-236.24, 75.14) * mm, v(-242.7, 72.06) * mm, v(-244.52, 78.23) * mm, v(-244.38, 87.77) * mm, v(-241.15, 89.31) * mm, v(-234, 91.13) * mm, v(-230.77, 82.72) * mm, v(-219.83, 73.46) * mm, v(-223.76, 69.67) * mm, v(-228.8, 73.74) * mm]});
            skFitSpline(sketch, "E131", {"points": [v(-222.36, 89.03) * mm, v(-224.6, 82.44) * mm, v(-218.7, 77.95) * mm, v(-213.8, 71.08) * mm, v(-206.37, 65.33) * mm, v(-200.06, 67) * mm, v(-204.96, 74.02) * mm, v(-215.62, 81.6) * mm, v(-213.24, 86.65) * mm, v(-211.7, 97.45) * mm, v(-222.36, 89.03) * mm]});
            skFitSpline(sketch, "E132", {"points": [v(-220.67, 96.32) * mm, v(-224.6, 95.9) * mm, v(-223.62, 101.8) * mm, v(-220.4, 105.58) * mm, v(-207.63, 103.62) * mm, v(-200.2, 98.15) * mm, v(-199.92, 85.24) * mm, v(-206.23, 81.74) * mm, v(-206.09, 89.45) * mm, v(-205.1, 96.46) * mm, v(-211.84, 100.95) * mm, v(-220.67, 96.32) * mm]});
            skFitSpline(sketch, "E133", {"points": [v(-197.67, 71.92) * mm, v(-194.3, 66.17) * mm, v(-185.19, 64.77) * mm, v(-172.85, 67.43) * mm, v(-173.97, 74.58) * mm, v(-186.17, 71.5) * mm, v(-191.78, 78.37) * mm, v(-201.46, 79.91) * mm, v(-197.67, 71.92) * mm]});
            skFitSpline(sketch, "E134", {"points": [v(-194.02, 85.52) * mm, v(-169.9, 81.18) * mm, v(-167.8, 74.72) * mm, v(-157, 80.2) * mm, v(-162.33, 93.94) * mm, v(-170.46, 88.75) * mm, v(-186.17, 88.6) * mm, v(-186.17, 95.06) * mm, v(-189.12, 98) * mm, v(-195.15, 95.06) * mm, v(-194.02, 85.52) * mm]});
            skFitSpline(sketch, "E135", {"points": [v(-157.84, 98.43) * mm, v(-150.97, 86.5) * mm, v(-154.47, 74.3) * mm, v(-147.88, 66.59) * mm, v(-139.74, 66.73) * mm, v(-144.23, 76.4) * mm, v(-141.85, 84.12) * mm, v(-131.19, 76.27) * mm, v(-127.12, 81.32) * mm, v(-140.3, 93.52) * mm, v(-148.44, 100.81) * mm, v(-154.2, 101.65) * mm, v(-157.84, 98.43) * mm]});
            skFitSpline(sketch, "E136", {"points": [v(-120.39, 76.97) * mm, v(-127.68, 72.48) * mm, v(-134.27, 72.2) * mm, v(-129.93, 65.75) * mm, v(-117.72, 65.33) * mm, v(-113.94, 78.37) * mm, v(-120.39, 76.97) * mm]});
            skFitSpline(sketch, "E137", {"points": [v(-141.05, 99) * mm, v(-142.24, 106.38) * mm, v(-136.53, 112.18) * mm, v(-127.97, 121.08) * mm, v(-117.38, 116.04) * mm, v(-101.33, 99.74) * mm, v(-118.8, 84.33) * mm, v(-120.63, 90.53) * mm, v(-112.3, 97.85) * mm, v(-118.46, 105.15) * mm, v(-125.7, 108.72) * mm, v(-126.34, 92.27) * mm, v(-141.05, 99) * mm]});
            skFitSpline(sketch, "E138", {"points": [v(-109.75, 73.77) * mm, v(-93.2, 76.7) * mm, v(-82.7, 68.09) * mm, v(-78.03, 72.53) * mm, v(-81.44, 78.57) * mm, v(-74.63, 80.97) * mm, v(-80.37, 89.06) * mm, v(-90.67, 89.93) * mm, v(-106.73, 83.21) * mm, v(-109.75, 73.77) * mm]});
            skFitSpline(sketch, "E139", {"points": [v(-83.15, 96.88) * mm, v(-90.9, 96.09) * mm, v(-95.45, 104.54) * mm, v(-98.4, 113.35) * mm, v(-101.36, 121.37) * mm, v(-92.34, 124.9) * mm, v(-87.06, 114.05) * mm, v(-78.8, 103.9) * mm, v(-83.15, 96.88) * mm]});
            skFitSpline(sketch, "E140", {"points": [v(-94.61, 128.93) * mm, v(-102.8, 127.36) * mm, v(-105.21, 118.3) * mm, v(-112.55, 118.5) * mm, v(-114.7, 127.68) * mm, v(-105.9, 137.57) * mm, v(-94, 144.8) * mm, v(-88.14, 149) * mm, v(-78, 149.53) * mm, v(-86.02, 138.82) * mm, v(-86.45, 129.9) * mm, v(-94.61, 128.93) * mm]});
            skCircle(sketch, "E141", {"center": v(-31.57, 88.37) * mm, "radius": 15.31 * mm});
            skCircle(sketch, "E142", {"center": v(-68.3, 125.46) * mm, "radius": 15.31 * mm});
            skCircle(sketch, "E143", {"center": v(-15.1, 133.37) * mm, "radius": 15.31 * mm});
            skCircle(sketch, "E144", {"center": v(18.97, 93.18) * mm, "radius": 15.31 * mm});
            skFitSpline(sketch, "E145", {"points": [v(-69.32, 147.51) * mm, v(-64.71, 156.72) * mm, v(-50.82, 149) * mm, v(-40, 137.8) * mm, v(-39.54, 125.1) * mm, v(-48.49, 132.08) * mm, v(-57.81, 147.4) * mm, v(-61.97, 147.91) * mm, v(-67.06, 142.89) * mm, v(-69.32, 147.51) * mm]});
            skFitSpline(sketch, "E146", {"points": [v(-51.3, 115.48) * mm, v(-49.7, 123.57) * mm, v(-44.18, 122.24) * mm, v(-40.86, 112.43) * mm, v(-22.94, 114.73) * mm, v(-8.23, 115.53) * mm, v(-9.5, 97.1) * mm, v(-16.78, 99.88) * mm, v(-28.5, 106.74) * mm, v(-44.86, 103.6) * mm, v(-51.3, 115.48) * mm]});
            skFitSpline(sketch, "E147", {"points": [v(-72.77, 99.18) * mm, v(-70.82, 105.48) * mm, v(-58.22, 109.11) * mm, v(-52.41, 103.4) * mm, v(-59.3, 97.83) * mm, v(-65.4, 92.44) * mm, v(-60.7, 82.4) * mm, v(-53.92, 76.06) * mm, v(-59.4, 71.64) * mm, v(-69.55, 77.86) * mm, v(-72.77, 99.18) * mm]});
            skFitSpline(sketch, "E148", {"points": [v(-29.15, 51.59) * mm, v(-21.2, 52.37) * mm, v(-19.27, 57.68) * mm, v(-41.07, 66.4) * mm, v(-42.74, 70.8) * mm, v(-35.8, 70.82) * mm, v(-26.32, 68.98) * mm, v(-15.46, 74.44) * mm, v(-7.72, 66.9) * mm, v(-8.63, 54.82) * mm, v(-10.13, 42.95) * mm, v(-16.52, 41.53) * mm, v(-23.8, 44.1) * mm, v(-29.15, 51.59) * mm]});
            skFitSpline(sketch, "E149", {"points": [v(-4.36, 46.69) * mm, v(4.84, 54.47) * mm, v(-6.72, 72.64) * mm, v(-13.33, 86.55) * mm, v(-6.25, 91.5) * mm, v(3.42, 81.13) * mm, v(9.55, 66.97) * mm, v(19.22, 48.81) * mm, v(15.45, 28.53) * mm, v(3.18, 25.22) * mm, v(6.72, 36.55) * mm, v(4.36, 38.2) * mm, v(-5.54, 22.63) * mm, v(-10.5, 22.63) * mm, v(-8.61, 30.88) * mm, v(-4.36, 46.69) * mm]});
            skFitSpline(sketch, "E150", {"points": [v(-33.85, 143.64) * mm, v(-25.36, 150.48) * mm, v(-12.38, 153.78) * mm, v(-13.8, 160.38) * mm, v(-31.02, 162.98) * mm, v(-49.18, 161.33) * mm, v(-49.18, 154.72) * mm, v(-39.51, 151.9) * mm, v(-37.62, 145.76) * mm, v(-33.85, 143.64) * mm]});
            skFitSpline(sketch, "E151", {"points": [v(2.7, 142.69) * mm, v(0, 147.05) * mm, v(-6.62, 150.23) * mm, v(-7.8, 157.37) * mm, v(1.91, 157.37) * mm, v(9.65, 150.82) * mm, v(11.03, 139.52) * mm, v(8.46, 125.83) * mm, v(3.1, 115.51) * mm, v(-1.86, 116.7) * mm, v(2.1, 128.8) * mm, v(2.7, 142.69) * mm]});
            skFitSpline(sketch, "E152", {"points": [v(17.58, 136.14) * mm, v(13.81, 143.88) * mm, v(15.6, 149.63) * mm, v(26.1, 148.84) * mm, v(37.02, 139.32) * mm, v(29.48, 138.13) * mm, v(24.13, 142.3) * mm, v(19.56, 139.52) * mm, v(19.96, 137.13) * mm, v(17.58, 136.14) * mm]});
            skFitSpline(sketch, "E153", {"points": [v(11.23, 114.32) * mm, v(10.84, 123.05) * mm, v(17.38, 130.2) * mm, v(28.1, 132.97) * mm, v(39.2, 131.18) * mm, v(38.2, 125.23) * mm, v(29.48, 123.65) * mm, v(19.17, 120.08) * mm, v(22.34, 115.91) * mm, v(31.27, 118.3) * mm, v(38.2, 117.7) * mm, v(36.03, 111.35) * mm, v(24.13, 109.56) * mm, v(11.23, 114.32) * mm]});
            skFitSpline(sketch, "E154", {"points": [v(38.01, 103.6) * mm, v(41.78, 112.14) * mm, v(42.18, 121.07) * mm, v(51.1, 126.03) * mm, v(57.25, 118.1) * mm, v(67.96, 100.64) * mm, v(59.04, 96.27) * mm, v(56.26, 103.6) * mm, v(46.14, 103.6) * mm, v(41.38, 100.04) * mm, v(38.01, 103.6) * mm]});
            skFitSpline(sketch, "E155", {"points": [v(25.68, 54.54) * mm, v(17.55, 65.2) * mm, v(15.3, 72.5) * mm, v(21.2, 72.21) * mm, v(29.33, 68.29) * mm, v(33.82, 78.95) * mm, v(39.43, 88.48) * mm, v(47.28, 95.5) * mm, v(55.42, 89.89) * mm, v(48.69, 80.63) * mm, v(51.77, 66.32) * mm, v(45.04, 51.59) * mm, v(25.68, 54.54) * mm]});
            skFitSpline(sketch, "E156", {"points": [v(67.48, 84.84) * mm, v(60.19, 78.1) * mm, v(58.22, 67.73) * mm, v(64.4, 56.79) * mm, v(59.35, 43.04) * mm, v(46.16, 43.32) * mm, v(45.32, 32.38) * mm, v(59.07, 30.98) * mm, v(84.6, 33.78) * mm, v(82.63, 40.52) * mm, v(80.95, 47.8) * mm, v(71.4, 62.68) * mm, v(69.45, 71.37) * mm, v(75.34, 78.95) * mm, v(74.5, 90.45) * mm, v(69.45, 92.13) * mm, v(67.48, 84.84) * mm]});
            skFitSpline(sketch, "E157", {"points": [v(20.35, 21.72) * mm, v(27.65, 29.58) * mm, v(27.65, 41.64) * mm, v(36.34, 43.04) * mm, v(35.5, 33.22) * mm, v(43.92, 22.56) * mm, v(52.33, 22) * mm, v(53.46, 15.27) * mm, v(46.16, 11.62) * mm, v(36.9, 8.54) * mm, v(37.75, -4.09) * mm, v(28.2, -7.45) * mm, v(30.73, 4.33) * mm, v(24.84, 13.3) * mm, v(9.98, 6.85) * mm, v(4.37, 12.75) * mm, v(20.35, 21.72) * mm]});
            skFitSpline(sketch, "E158", {"points": [v(-14.43, 30.42) * mm, v(-18.64, 36.3) * mm, v(-26.5, 33.78) * mm, v(-25.93, 18.08) * mm, v(-29.15, 9.66) * mm, v(-18.36, 4.61) * mm, v(-2.93, 5.73) * mm, v(-4.9, 12.75) * mm, v(-16.4, 13.3) * mm, v(-17.8, 20.88) * mm, v(-14.43, 30.42) * mm]});
            skFitSpline(sketch, "E159", {"points": [v(66.08, 5.45) * mm, v(63, 23.12) * mm, v(79.54, 15.27) * mm, v(88.52, -8.57) * mm, v(85.43, -25.97) * mm, v(70.85, -37.47) * mm, v(50.09, -34.38) * mm, v(53.46, -26.53) * mm, v(72.25, -20.36) * mm, v(74.77, -7.17) * mm, v(66.08, 5.45) * mm]});
            skFitSpline(sketch, "E160", {"points": [v(22.04, 0) * mm, v(21.2, -18.67) * mm, v(37.19, -17.55) * mm, v(38.3, -35.78) * mm, v(51.21, -49.8) * mm, v(66.36, -48.69) * mm, v(76.18, -60.47) * mm, v(62.43, -68.6) * mm, v(45.88, -60.75) * mm, v(29.33, -47.85) * mm, v(29.05, -36.9) * mm, v(18.4, -31.02) * mm, v(4.37, -18.67) * mm, v(7.17, -5.2) * mm, v(22.04, 0) * mm]});
            skFitSpline(sketch, "E161", {"points": [v(50.09, -11.66) * mm, v(56.82, -14.18) * mm, v(61.03, -8.3) * mm, v(57.1, 4.05) * mm, v(49.8, -5.49) * mm, v(50.09, -11.66) * mm]});
            skFitSpline(sketch, "E162", {"points": [v(-28.74, -10.54) * mm, v(-18.08, -24.56) * mm, v(-21.44, -45.88) * mm, v(-10.22, -55.42) * mm, v(3.8, -43.64) * mm, v(4.65, -31.86) * mm, v(-4.61, -24) * mm, v(-3.49, -13.06) * mm, v(-13.87, -4.65) * mm, v(-24.25, -2.96) * mm, v(-30.14, -6.33) * mm, v(-28.74, -10.54) * mm]});
            skFitSpline(sketch, "E163", {"points": [v(-4.84, -64.9) * mm, v(5.26, -57.88) * mm, v(12, -44.14) * mm, v(16.76, -40.5) * mm, v(20.97, -44.7) * mm, v(19.85, -53.68) * mm, v(24.05, -59.57) * mm, v(34.43, -62.93) * mm, v(47.9, -78.92) * mm, v(37.24, -78.38) * mm, v(26.02, -69.95) * mm, v(12, -68.26) * mm, v(-3.44, -72.2) * mm, v(-10.73, -70.23) * mm, v(-4.84, -64.9) * mm]});
            skFitSpline(sketch, "E164", {"points": [v(56.03, -83.97) * mm, v(54.63, -77.52) * mm, v(60.8, -74.44) * mm, v(67.25, -78.08) * mm, v(68.38, -88.18) * mm, v(61.64, -92.39) * mm, v(56.03, -83.97) * mm]});
            skFitSpline(sketch, "E165", {"points": [v(45.1, -115.67) * mm, v(53.23, -108.1) * mm, v(54.07, -99.12) * mm, v(49.3, -92.39) * mm, v(39.76, -92.95) * mm, v(37.24, -101.36) * mm, v(29.33, -109.22) * mm, v(20.97, -104.17) * mm, v(23.21, -91.83) * mm, v(15.64, -85.94) * mm, v(2.46, -90.99) * mm, v(3.02, -99.68) * mm, v(16.76, -117.07) * mm, v(29.33, -120.72) * mm, v(45.1, -115.67) * mm]});
            skFitSpline(sketch, "E166", {"points": [v(-5.68, -96.32) * mm, v(-6.24, -90.14) * mm, v(0, -84.81) * mm, v(-2.6, -78.38) * mm, v(-12.41, -78.38) * mm, v(-21.1, -74.72) * mm, v(-28.68, -60.97) * mm, v(-29.24, -52.56) * mm, v(-36.26, -47.85) * mm, v(-42.43, -57.32) * mm, v(-37.94, -72.47) * mm, v(-31.2, -82.85) * mm, v(-24.2, -94.07) * mm, v(-11.57, -99.4) * mm, v(-5.68, -96.32) * mm]});
            skFitSpline(sketch, "E167", {"points": [v(-25.06, -107.17) * mm, v(-19.4, -105.52) * mm, v(-11.38, -106.23) * mm, v(-4.54, -106.23) * mm, v(2.3, -112.84) * mm, v(5.37, -124.87) * mm, v(0, -137.13) * mm, v(-9.73, -144.92) * mm, v(-24.12, -146.33) * mm, v(-35.2, -140.9) * mm, v(-38.03, -128.88) * mm, v(-34.5, -114.25) * mm, v(-25.06, -107.17) * mm]});
            skFitSpline(sketch, "E168", {"points": [v(-55.25, -141.38) * mm, v(-47.23, -143.74) * mm, v(-42.51, -139.02) * mm, v(-47.7, -131.47) * mm, v(-47.47, -120.62) * mm, v(-41.57, -117.55) * mm, v(-43.93, -108.59) * mm, v(-58.08, -107.65) * mm, v(-68.93, -112.13) * mm, v(-69.17, -121.8) * mm, v(-55.25, -141.38) * mm]});
            skFitSpline(sketch, "E169", {"points": [v(-65.87, -98.68) * mm, v(-46.05, -98.92) * mm, v(-40.16, -104.34) * mm, v(-30.72, -100.1) * mm, v(-41.57, -88.78) * mm, v(-56.9, -86.89) * mm, v(-69.4, -89.25) * mm, v(-65.87, -98.68) * mm]});
            skFitSpline(sketch, "E170", {"points": [v(-54.3, -55.52) * mm, v(-69.17, -63.06) * mm, v(-71.53, -78.38) * mm, v(-64.92, -81.46) * mm, v(-58.32, -76.04) * mm, v(-48.65, -78.38) * mm, v(-41.8, -78.38) * mm, v(-42.75, -75.57) * mm, v(-52.19, -71.8) * mm, v(-55.25, -63.54) * mm, v(-48.65, -56.46) * mm, v(-49.83, -51.98) * mm, v(-54.3, -55.52) * mm]});
            skFitSpline(sketch, "E171", {"points": [v(-91.58, -127.93) * mm, v(-82.85, -133.36) * mm, v(-73.89, -137.37) * mm, v(-68.23, -138.31) * mm, v(-69.88, -133.6) * mm, v(-76.95, -128.64) * mm, v(-82.85, -120.86) * mm, v(-80.02, -112.84) * mm, v(-76.72, -109.06) * mm, v(-81.67, -101.99) * mm, v(-97, -111.18) * mm, v(-111.4, -107.41) * mm, v(-114.7, -112.84) * mm, v(-91.58, -127.93) * mm]});
            skFitSpline(sketch, "E172", {"points": [v(-98.63, -103.63) * mm, v(-86.57, -94.65) * mm, v(-78.15, -87.64) * mm, v(-82.64, -78.38) * mm, v(-95.82, -78.38) * mm, v(-104.8, -70.24) * mm, v(-114.9, -70.52) * mm, v(-111.53, -82.87) * mm, v(-113.22, -94.37) * mm, v(-98.63, -103.63) * mm]});
            skFitSpline(sketch, "E173", {"points": [v(-141.83, -87.92) * mm, v(-130.05, -101.39) * mm, v(-122.47, -103.63) * mm, v(-123.31, -92.97) * mm, v(-120.8, -83.43) * mm, v(-128.36, -76.7) * mm, v(-141.83, -87.92) * mm]});
            skFitSpline(sketch, "E174", {"points": [v(-129.49, -68.56) * mm, v(-116.3, -63.22) * mm, v(-102.56, -65.47) * mm, v(-95.26, -72.2) * mm, v(-83.76, -73.05) * mm, v(-79, -63.22) * mm, v(-68.9, -55.93) * mm, v(-62.72, -47.85) * mm, v(-71.42, -42.18) * mm, v(-86.85, -47.85) * mm, v(-92.74, -57.33) * mm, v(-107.89, -52) * mm, v(-111.25, -43.3) * mm, v(-124.72, -41.34) * mm, v(-139.02, -47.85) * mm, v(-123.31, -51.16) * mm, v(-123.03, -57.05) * mm, v(-136.5, -58.73) * mm, v(-142.67, -68.56) * mm, v(-129.49, -68.56) * mm]});
            skFitSpline(sketch, "E175", {"points": [v(-163.43, -75.3) * mm, v(-151.09, -82.87) * mm, v(-144.63, -78.38) * mm, v(-150.24, -70.24) * mm, v(-151.37, -59.3) * mm, v(-146.04, -54.52) * mm, v(-148.84, -45.26) * mm, v(-161.47, -43.02) * mm, v(-173.8, -55.37) * mm, v(-163.43, -75.3) * mm]});
            skFitSpline(sketch, "E176", {"points": [v(-176.33, -47.85) * mm, v(-181.38, -57.05) * mm, v(-194.57, -56.77) * mm, v(-195.69, -47.85) * mm, v(-186.43, -41.05) * mm, v(-178.3, -39.93) * mm, v(-174.09, -43.58) * mm, v(-176.33, -47.85) * mm]});
            skFitSpline(sketch, "E177", {"points": [v(-207.47, -56.49) * mm, v(-198.5, -60.7) * mm, v(-186.71, -62.1) * mm, v(-180, -62.87) * mm, v(-177.45, -68.56) * mm, v(-184.75, -74.17) * mm, v(-199.33, -76.97) * mm, v(-212.8, -81.74) * mm, v(-220.37, -78.38) * mm, v(-215.04, -73.05) * mm, v(-201.86, -71.36) * mm, v(-205.79, -66.87) * mm, v(-220.65, -63.5) * mm, v(-225.98, -55.37) * mm, v(-241.97, -45.54) * mm, v(-234.68, -40.77) * mm, v(-220.1, -47.85) * mm, v(-210.27, -42.18) * mm, v(-203.82, -42.74) * mm, v(-207.47, -56.49) * mm]});
            skFitSpline(sketch, "E178", {"points": [v(-318.27, -63.22) * mm, v(-311.54, -53.96) * mm, v(-319.11, -47.85) * mm, v(-326.69, -47.85) * mm, v(-328.1, -42.74) * mm, v(-320.24, -40.21) * mm, v(-305.93, -39.93) * mm, v(-300.6, -47.85) * mm, v(-287.98, -47.85) * mm, v(-284.61, -41.9) * mm, v(-275.35, -47.85) * mm, v(-278.44, -59.01) * mm, v(-289.1, -60.42) * mm, v(-300.6, -61.26) * mm, v(-306.5, -68.84) * mm, v(-303.13, -78.38) * mm, v(-313.5, -78.38) * mm, v(-318.27, -63.22) * mm]});
            skFitSpline(sketch, "E179", {"points": [v(-288.26, -93.25) * mm, v(-297.51, -90.16) * mm, v(-295.55, -85.4) * mm, v(-284.05, -85.11) * mm, v(-273.67, -82.87) * mm, v(-271.43, -73.33) * mm, v(-273.67, -65.19) * mm, v(-269.74, -58.73) * mm, v(-268.62, -47.85) * mm, v(-260.77, -47.85) * mm, v(-260.77, -60.98) * mm, v(-264.7, -70.24) * mm, v(-261.6, -78.38) * mm, v(-266.66, -91.85) * mm, v(-253.2, -89.32) * mm, v(-241.41, -88.2) * mm, v(-242.53, -98.68) * mm, v(-259.65, -101.1) * mm, v(-272.83, -96.34) * mm, v(-288.26, -93.25) * mm]});
            skFitSpline(sketch, "E180", {"points": [v(-252.07, -78.38) * mm, v(-253.75, -68.56) * mm, v(-250.95, -59.3) * mm, v(-251.23, -51.16) * mm, v(-241.41, -55.93) * mm, v(-233, -65.75) * mm, v(-231.31, -75.85) * mm, v(-226.54, -83.99) * mm, v(-230.47, -91.85) * mm, v(-235.8, -85.67) * mm, v(-239.45, -75.3) * mm, v(-245.62, -78.38) * mm, v(-252.07, -78.38) * mm]});
            skSolve(sketch);
        }
        {
            var Q0;
            Q0=makeQuery(id+"F4.imprint","IMPRINT",FACE,{"disambiguationData":[TD([[makeQuery(id+"F4.imprint","IMPRINT",EDGE,{"derivedFrom":sQuery(id+"F4.wireOp",EDGE,"E128")}),1.0]])]});
            var Q1;
            Q1=makeQuery(id+"F4.imprint","IMPRINT",FACE,{"disambiguationData":[TD([[makeQuery(id+"F4.imprint","IMPRINT",EDGE,{"derivedFrom":sQuery(id+"F4.wireOp",EDGE,"E127")}),1.0]])]});
            var Q2;
            Q2=makeQuery(id+"F4.imprint","IMPRINT",FACE,{"disambiguationData":[TD([[makeQuery(id+"F4.imprint","IMPRINT",EDGE,{"derivedFrom":sQuery(id+"F4.wireOp",EDGE,"E126")}),-1.0]])]});
            var Q3;
            Q3=makeQuery(id+"F4.imprint","IMPRINT",FACE,{"disambiguationData":[TD([[makeQuery(id+"F4.imprint","IMPRINT",EDGE,{"derivedFrom":sQuery(id+"F4.wireOp",EDGE,"E129")}),-1.0]])]});
            var Q4;
            Q4=makeQuery(id+"F4.imprint","IMPRINT",FACE,{"disambiguationData":[TD([[makeQuery(id+"F4.imprint","IMPRINT",EDGE,{"derivedFrom":sQuery(id+"F4.wireOp",EDGE,"E130")}),-1.0]])]});
            var Q5;
            Q5=makeQuery(id+"F4.imprint","IMPRINT",FACE,{"disambiguationData":[TD([[makeQuery(id+"F4.imprint","IMPRINT",EDGE,{"derivedFrom":sQuery(id+"F4.wireOp",EDGE,"E131")}),1.0]])]});
            var Q6;
            Q6=makeQuery(id+"F4.imprint","IMPRINT",FACE,{"disambiguationData":[TD([[makeQuery(id+"F4.imprint","IMPRINT",EDGE,{"derivedFrom":sQuery(id+"F4.wireOp",EDGE,"E132")}),-1.0]])]});
            var Q7;
            Q7=makeQuery(id+"F4.imprint","IMPRINT",FACE,{"disambiguationData":[TD([[makeQuery(id+"F4.imprint","IMPRINT",EDGE,{"derivedFrom":sQuery(id+"F4.wireOp",EDGE,"E134")}),1.0]])]});
            var Q8;
            Q8=makeQuery(id+"F4.imprint","IMPRINT",FACE,{"disambiguationData":[TD([[makeQuery(id+"F4.imprint","IMPRINT",EDGE,{"derivedFrom":sQuery(id+"F4.wireOp",EDGE,"E133")}),1.0]])]});
            var Q9;
            Q9=makeQuery(id+"F4.imprint","IMPRINT",FACE,{"disambiguationData":[TD([[makeQuery(id+"F4.imprint","IMPRINT",EDGE,{"derivedFrom":sQuery(id+"F4.wireOp",EDGE,"E135")}),1.0]])]});
            var Q10;
            Q10=makeQuery(id+"F4.imprint","IMPRINT",FACE,{"disambiguationData":[TD([[makeQuery(id+"F4.imprint","IMPRINT",EDGE,{"derivedFrom":sQuery(id+"F4.wireOp",EDGE,"E136")}),1.0]])]});
            var Q11;
            Q11=makeQuery(id+"F4.imprint","IMPRINT",FACE,{"disambiguationData":[TD([[makeQuery(id+"F4.imprint","IMPRINT",EDGE,{"derivedFrom":sQuery(id+"F4.wireOp",EDGE,"E137")}),-1.0]])]});
            var Q12;
            Q12=makeQuery(id+"F4.imprint","IMPRINT",FACE,{"disambiguationData":[TD([[makeQuery(id+"F4.imprint","IMPRINT",EDGE,{"derivedFrom":sQuery(id+"F4.wireOp",EDGE,"E138")}),1.0]])]});
            var Q13;
            Q13=makeQuery(id+"F4.imprint","IMPRINT",FACE,{"disambiguationData":[TD([[makeQuery(id+"F4.imprint","IMPRINT",EDGE,{"derivedFrom":sQuery(id+"F4.wireOp",EDGE,"E139")}),-1.0]])]});
            var Q14;
            Q14=makeQuery(id+"F4.imprint","IMPRINT",FACE,{"disambiguationData":[TD([[makeQuery(id+"F4.imprint","IMPRINT",EDGE,{"derivedFrom":sQuery(id+"F4.wireOp",EDGE,"E140")}),-1.0]])]});
            var Q15;
            Q15=makeQuery(id+"F4.imprint","IMPRINT",FACE,{"disambiguationData":[TD([[makeQuery(id+"F4.imprint","IMPRINT",EDGE,{"derivedFrom":sQuery(id+"F4.wireOp",EDGE,"E145")}),-1.0]])]});
            var Q16;
            Q16=makeQuery(id+"F4.imprint","IMPRINT",FACE,{"disambiguationData":[TD([[makeQuery(id+"F4.imprint","IMPRINT",EDGE,{"derivedFrom":sQuery(id+"F4.wireOp",EDGE,"E150")}),1.0]])]});
            var Q17;
            Q17=makeQuery(id+"F4.imprint","IMPRINT",FACE,{"disambiguationData":[TD([[makeQuery(id+"F4.imprint","IMPRINT",EDGE,{"derivedFrom":sQuery(id+"F4.wireOp",EDGE,"E151")}),-1.0]])]});
            var Q18;
            Q18=makeQuery(id+"F4.imprint","IMPRINT",FACE,{"disambiguationData":[TD([[makeQuery(id+"F4.imprint","IMPRINT",EDGE,{"derivedFrom":sQuery(id+"F4.wireOp",EDGE,"E152")}),-1.0]])]});
            var Q19;
            Q19=makeQuery(id+"F4.imprint","IMPRINT",FACE,{"disambiguationData":[TD([[makeQuery(id+"F4.imprint","IMPRINT",EDGE,{"derivedFrom":sQuery(id+"F4.wireOp",EDGE,"E153")}),-1.0]])]});
            var Q20;
            Q20=makeQuery(id+"F4.imprint","IMPRINT",FACE,{"disambiguationData":[TD([[makeQuery(id+"F4.imprint","IMPRINT",EDGE,{"derivedFrom":sQuery(id+"F4.wireOp",EDGE,"E154")}),-1.0]])]});
            var Q21;
            Q21=makeQuery(id+"F4.imprint","IMPRINT",FACE,{"disambiguationData":[TD([[makeQuery(id+"F4.imprint","IMPRINT",EDGE,{"derivedFrom":sQuery(id+"F4.wireOp",EDGE,"E146")}),-1.0]])]});
            var Q22;
            Q22=makeQuery(id+"F4.imprint","IMPRINT",FACE,{"disambiguationData":[TD([[makeQuery(id+"F4.imprint","IMPRINT",EDGE,{"derivedFrom":sQuery(id+"F4.wireOp",EDGE,"E147")}),-1.0]])]});
            var Q23;
            Q23=makeQuery(id+"F4.imprint","IMPRINT",FACE,{"disambiguationData":[TD([[makeQuery(id+"F4.imprint","IMPRINT",EDGE,{"derivedFrom":sQuery(id+"F4.wireOp",EDGE,"E148")}),-1.0]])]});
            var Q24;
            Q24=makeQuery(id+"F4.imprint","IMPRINT",FACE,{"disambiguationData":[TD([[makeQuery(id+"F4.imprint","IMPRINT",EDGE,{"derivedFrom":sQuery(id+"F4.wireOp",EDGE,"E149")}),-1.0]])]});
            var Q25;
            Q25=makeQuery(id+"F4.imprint","IMPRINT",FACE,{"disambiguationData":[TD([[makeQuery(id+"F4.imprint","IMPRINT",EDGE,{"derivedFrom":sQuery(id+"F4.wireOp",EDGE,"E155")}),-1.0]])]});
            var Q26;
            Q26=makeQuery(id+"F4.imprint","IMPRINT",FACE,{"disambiguationData":[TD([[makeQuery(id+"F4.imprint","IMPRINT",EDGE,{"derivedFrom":sQuery(id+"F4.wireOp",EDGE,"E156")}),1.0]])]});
            var Q27;
            Q27=makeQuery(id+"F4.imprint","IMPRINT",FACE,{"disambiguationData":[TD([[makeQuery(id+"F4.imprint","IMPRINT",EDGE,{"derivedFrom":sQuery(id+"F4.wireOp",EDGE,"E157")}),-1.0]])]});
            var Q28;
            Q28=makeQuery(id+"F4.imprint","IMPRINT",FACE,{"disambiguationData":[TD([[makeQuery(id+"F4.imprint","IMPRINT",EDGE,{"derivedFrom":sQuery(id+"F4.wireOp",EDGE,"E158")}),1.0]])]});
            var Q29;
            Q29=makeQuery(id+"F4.imprint","IMPRINT",FACE,{"disambiguationData":[TD([[makeQuery(id+"F4.imprint","IMPRINT",EDGE,{"derivedFrom":sQuery(id+"F4.wireOp",EDGE,"E161")}),1.0]])]});
            var Q30;
            Q30=makeQuery(id+"F4.imprint","IMPRINT",FACE,{"disambiguationData":[TD([[makeQuery(id+"F4.imprint","IMPRINT",EDGE,{"derivedFrom":sQuery(id+"F4.wireOp",EDGE,"E159")}),-1.0]])]});
            var Q31;
            Q31=makeQuery(id+"F4.imprint","IMPRINT",FACE,{"disambiguationData":[TD([[makeQuery(id+"F4.imprint","IMPRINT",EDGE,{"derivedFrom":sQuery(id+"F4.wireOp",EDGE,"E160")}),-1.0]])]});
            var Q32;
            Q32=makeQuery(id+"F4.imprint","IMPRINT",FACE,{"disambiguationData":[TD([[makeQuery(id+"F4.imprint","IMPRINT",EDGE,{"derivedFrom":sQuery(id+"F4.wireOp",EDGE,"E162")}),1.0]])]});
            var Q33;
            Q33=makeQuery(id+"F4.imprint","IMPRINT",FACE,{"disambiguationData":[TD([[makeQuery(id+"F4.imprint","IMPRINT",EDGE,{"derivedFrom":sQuery(id+"F4.wireOp",EDGE,"E163")}),-1.0]])]});
            var Q34;
            Q34=makeQuery(id+"F4.imprint","IMPRINT",FACE,{"disambiguationData":[TD([[makeQuery(id+"F4.imprint","IMPRINT",EDGE,{"derivedFrom":sQuery(id+"F4.wireOp",EDGE,"E164")}),-1.0]])]});
            var Q35;
            Q35=makeQuery(id+"F4.imprint","IMPRINT",FACE,{"disambiguationData":[TD([[makeQuery(id+"F4.imprint","IMPRINT",EDGE,{"derivedFrom":sQuery(id+"F4.wireOp",EDGE,"E165")}),1.0]])]});
            var Q36;
            Q36=makeQuery(id+"F4.imprint","IMPRINT",FACE,{"disambiguationData":[TD([[makeQuery(id+"F4.imprint","IMPRINT",EDGE,{"derivedFrom":sQuery(id+"F4.wireOp",EDGE,"E167")}),-1.0]])]});
            var Q37;
            Q37=makeQuery(id+"F4.imprint","IMPRINT",FACE,{"disambiguationData":[TD([[makeQuery(id+"F4.imprint","IMPRINT",EDGE,{"derivedFrom":sQuery(id+"F4.wireOp",EDGE,"E166")}),1.0]])]});
            var Q38;
            Q38=makeQuery(id+"F4.imprint","IMPRINT",FACE,{"disambiguationData":[TD([[makeQuery(id+"F4.imprint","IMPRINT",EDGE,{"derivedFrom":sQuery(id+"F4.wireOp",EDGE,"E170")}),1.0]])]});
            var Q39;
            Q39=makeQuery(id+"F4.imprint","IMPRINT",FACE,{"disambiguationData":[TD([[makeQuery(id+"F4.imprint","IMPRINT",EDGE,{"derivedFrom":sQuery(id+"F4.wireOp",EDGE,"E169")}),1.0]])]});
            var Q40;
            Q40=makeQuery(id+"F4.imprint","IMPRINT",FACE,{"disambiguationData":[TD([[makeQuery(id+"F4.imprint","IMPRINT",EDGE,{"derivedFrom":sQuery(id+"F4.wireOp",EDGE,"E168")}),1.0]])]});
            var Q41;
            Q41=makeQuery(id+"F4.imprint","IMPRINT",FACE,{"disambiguationData":[TD([[makeQuery(id+"F4.imprint","IMPRINT",EDGE,{"derivedFrom":sQuery(id+"F4.wireOp",EDGE,"E171")}),1.0]])]});
            var Q42;
            Q42=makeQuery(id+"F4.imprint","IMPRINT",FACE,{"disambiguationData":[TD([[makeQuery(id+"F4.imprint","IMPRINT",EDGE,{"derivedFrom":sQuery(id+"F4.wireOp",EDGE,"E172")}),1.0]])]});
            var Q43;
            Q43=makeQuery(id+"F4.imprint","IMPRINT",FACE,{"disambiguationData":[TD([[makeQuery(id+"F4.imprint","IMPRINT",EDGE,{"derivedFrom":sQuery(id+"F4.wireOp",EDGE,"E174")}),1.0]])]});
            var Q44;
            Q44=makeQuery(id+"F4.imprint","IMPRINT",FACE,{"disambiguationData":[TD([[makeQuery(id+"F4.imprint","IMPRINT",EDGE,{"derivedFrom":sQuery(id+"F4.wireOp",EDGE,"E173")}),1.0]])]});
            var Q45;
            Q45=makeQuery(id+"F4.imprint","IMPRINT",FACE,{"disambiguationData":[TD([[makeQuery(id+"F4.imprint","IMPRINT",EDGE,{"derivedFrom":sQuery(id+"F4.wireOp",EDGE,"E175")}),1.0]])]});
            var Q46;
            Q46=makeQuery(id+"F4.imprint","IMPRINT",FACE,{"disambiguationData":[TD([[makeQuery(id+"F4.imprint","IMPRINT",EDGE,{"derivedFrom":sQuery(id+"F4.wireOp",EDGE,"E176")}),-1.0]])]});
            var Q47;
            Q47=makeQuery(id+"F4.imprint","IMPRINT",FACE,{"disambiguationData":[TD([[makeQuery(id+"F4.imprint","IMPRINT",EDGE,{"derivedFrom":sQuery(id+"F4.wireOp",EDGE,"E177")}),-1.0]])]});
            var Q48;
            Q48=makeQuery(id+"F4.imprint","IMPRINT",FACE,{"disambiguationData":[TD([[makeQuery(id+"F4.imprint","IMPRINT",EDGE,{"derivedFrom":sQuery(id+"F4.wireOp",EDGE,"E180")}),-1.0]])]});
            var Q49;
            Q49=makeQuery(id+"F4.imprint","IMPRINT",FACE,{"disambiguationData":[TD([[makeQuery(id+"F4.imprint","IMPRINT",EDGE,{"derivedFrom":sQuery(id+"F4.wireOp",EDGE,"E179")}),-1.0]])]});
            var Q50;
            Q50=makeQuery(id+"F4.imprint","IMPRINT",FACE,{"disambiguationData":[TD([[makeQuery(id+"F4.imprint","IMPRINT",EDGE,{"derivedFrom":sQuery(id+"F4.wireOp",EDGE,"E178")}),-1.0]])]});
            extrude(context, id + "F5", {"entities" : qUnion([Q0, Q1, Q2, Q3, Q4, Q5, Q6, Q7, Q8, Q9, Q10, Q11, Q12, Q13, Q14, Q15, Q16, Q17, Q18, Q19, Q20, Q21, Q22, Q23, Q24, Q25, Q26, Q27, Q28, Q29, Q30, Q31, Q32, Q33, Q34, Q35, Q36, Q37, Q38, Q39, Q40, Q41, Q42, Q43, Q44, Q45, Q46, Q47, Q48, Q49, Q50]), "operationType" : NewBodyOperationType.REMOVE, "oppositeDirection" : true, "depth" : 25 * mm, "offsetDistance" : 25 * mm});
        }
        {
            var Q0;
            Q0=makeQuery(id+"F3.boolean.opBoolean","COPY",FACE,{"derivedFrom":makeQuery(id+"F3.opExtrude","SWEPT_FACE",FACE,{"disambiguationData":[OSD([sQuery(id+"F0.wireOp",EDGE,"E115.right")])]})});
            var sketch = newSketch(context, id + "F6", { "sketchPlane" : qUnion([Q0])});
            skCircle(sketch, "E181", {"center": v(-13.97, -20.78) * mm, "radius": 4 * mm});
            skSolve(sketch);
        }
        {
            var Q0;
            Q0 = qSketchRegion(id + "F6", true);
            extrude(context, id + "F7", {"entities" : qUnion([Q0]), "operationType" : NewBodyOperationType.REMOVE, "oppositeDirection" : true, "depth" : 70 * mm, "offsetDistance" : 25 * mm});
        }
        {
            var Q0;
            Q0=makeQuery(id+"F3.boolean.opBoolean","COPY",FACE,{"derivedFrom":makeQuery(id+"F3.opExtrude","SWEPT_FACE",FACE,{"disambiguationData":[OSD([sQuery(id+"F0.wireOp",EDGE,"E116.bottom")])]})});
            var sketch = newSketch(context, id + "F8", { "sketchPlane" : qUnion([Q0])});
            skCircle(sketch, "E182", {"center": v(-127.2, -21) * mm, "radius": 4 * mm});
            skSolve(sketch);
        }
        {
            var Q0;
            Q0 = qSketchRegion(id + "F8", true);
            extrude(context, id + "F9", {"entities" : qUnion([Q0]), "operationType" : NewBodyOperationType.REMOVE, "oppositeDirection" : true, "depth" : 25 * mm, "offsetDistance" : 25 * mm});
        }
        {
            var Q0;
            Q0=makeQuery(id+"F2.opExtrude","SWEPT_FACE",FACE,{"disambiguationData":[OSD([sQuery(id+"F0.wireOp",EDGE,"E9")])]});
            var sketch = newSketch(context, id + "F10", { "sketchPlane" : qUnion([Q0])});
            skCircle(sketch, "E183", {"center": v(45.26, -22.5) * mm, "radius": 3.25 * mm});
            skSolve(sketch);
        }
        {
            var Q0;
            Q0 = qSketchRegion(id + "F10", true);
            extrude(context, id + "F11", {"entities" : qUnion([Q0]), "operationType" : NewBodyOperationType.REMOVE, "oppositeDirection" : true, "depth" : 25 * mm, "offsetDistance" : 25 * mm});
        }
    });
